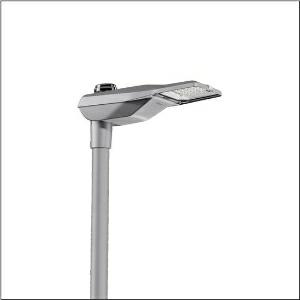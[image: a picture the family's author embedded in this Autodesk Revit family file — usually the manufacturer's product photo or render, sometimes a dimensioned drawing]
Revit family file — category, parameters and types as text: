
# Revit family: streetlight_sl_21_micro___st1_0a_5xe5d57n08db_813c
name_source: partatom
category: Lighting Fixtures
units: mm (PartAtom-declared; Revit-internal decimal feet)

## family parameters
Cut with Voids When Loaded = No
Host = Face
Light Source = No
Part Type = Normal
Room Calculation Point = No
Round Connector Dimension = Use Diameter
Shared = No

## types (1)
- --- (1 x LED, 4400 lm, 39.1 W, 3000K)
    Apparent Load = 39 VA
    CIE Flux Codes = 37 72 97 100 100
    Color Rendering = 80
    Color Temperature = 3000K
    Default Elevation = 1800 mm
    Description = Streetlight SL 21 micro, mast luminaire, primary light control with lens, of PMMA, primary optical cover: cover, of toughened safety glass, transparent, light distribution: ST1.0a, light emission: direct distribution, primary light characteristic: asymmetric, installation type: post-top, LED, 3G 1.5mm², High Power LED, rated luminous flux: 4.400lm, luminous efficacy: 113lm/W, light colour: 830, colour temperature: 3000K, control gear: NEMA (7pin), control: overheat protection, pre-setting: linear dimming characteristic, constant luminous flux control, time-dependent luminous flux control, flexible luminous flux parameterisation, mains connection: 230..240V, AC, 50/60Hz, connection cable pre-assembled, cable length: 6,5m, wiring characteristics: H07RN-F, start of lifetime: 39W, end of service life: 41W, reduction: 18W, luminaire housing, of diecast aluminium (EN AC-44300), powder-coated, SITECO metallic grey (DB 702S), corrosivity category C5 high according to DIN EN ISO 12944, multi-level sealing system, sealing non-destructively replaceable, inclination adjustable: 0°, 5°, 10°, 15°, length: 528mm, width: 235mm, height: 110mm, spigot size: 76/60mm (post-top), mounting height: 4..8m, protection rating (complete): IP66, insulation class (complete): insulation class I (protective earthing), certification: CE, ENEC, ENEC+, VDE, impact resistance: IK10, permissible operating ambient temperature for outdoor applications: -40..+50°C, standard-compliant lighting for roads and squares, packaging unit: 1 piece

Light Distribution: ST1.0a
    Height = 110 mm
    Lamp = 1 x LED
    Lamp Light Flux = 4400 lm
    Lamp Power = 39.1 W
    Lamp count = 1
    Length = 528 mm
    Luminous efficacy = 113 lm/W
    Manufacturer = Siteco
    ModVariant = No
    Model = 5XE5D57N08DB
    Number of Poles = 1
    OnlyDefault = Yes
    Power Factor = 1
    Product Name = Streetlight SL 21 micro | ST1.0a
    Product group = mast luminaire | pylon top
    ProductGroupID = 6100
    Protection Class = Protection class I
    Protection Degree = IP 66
    RLX_Detail_Level = 1
    RLX_Emergency_Light_Flux = 0 lm
    RLX_Emergency_Type = 0
    RLX_Emergency_Type_DB = No
    RlxData = <blob elided: 99085 chars, md5=a0163843>
    Socket = socket
    Standby Power = 0 W
    System Light Flux = 4400 lm
    System Power = 39 W
    Type Comments = factory setting: luminous flux: 100 % | dim-lin: 254 | 765 mA
    Type Image = l_1294375.jpg
    URL = http://relux.com
    VarID = @adj_135933
    Voltage = 0 V
    Weight = 0.00 kg
    Width = 235 mm

## geometry (parser evidence)
native form markers: Blend x4, Sweep x8
no freeform markers — native parametric forms only
